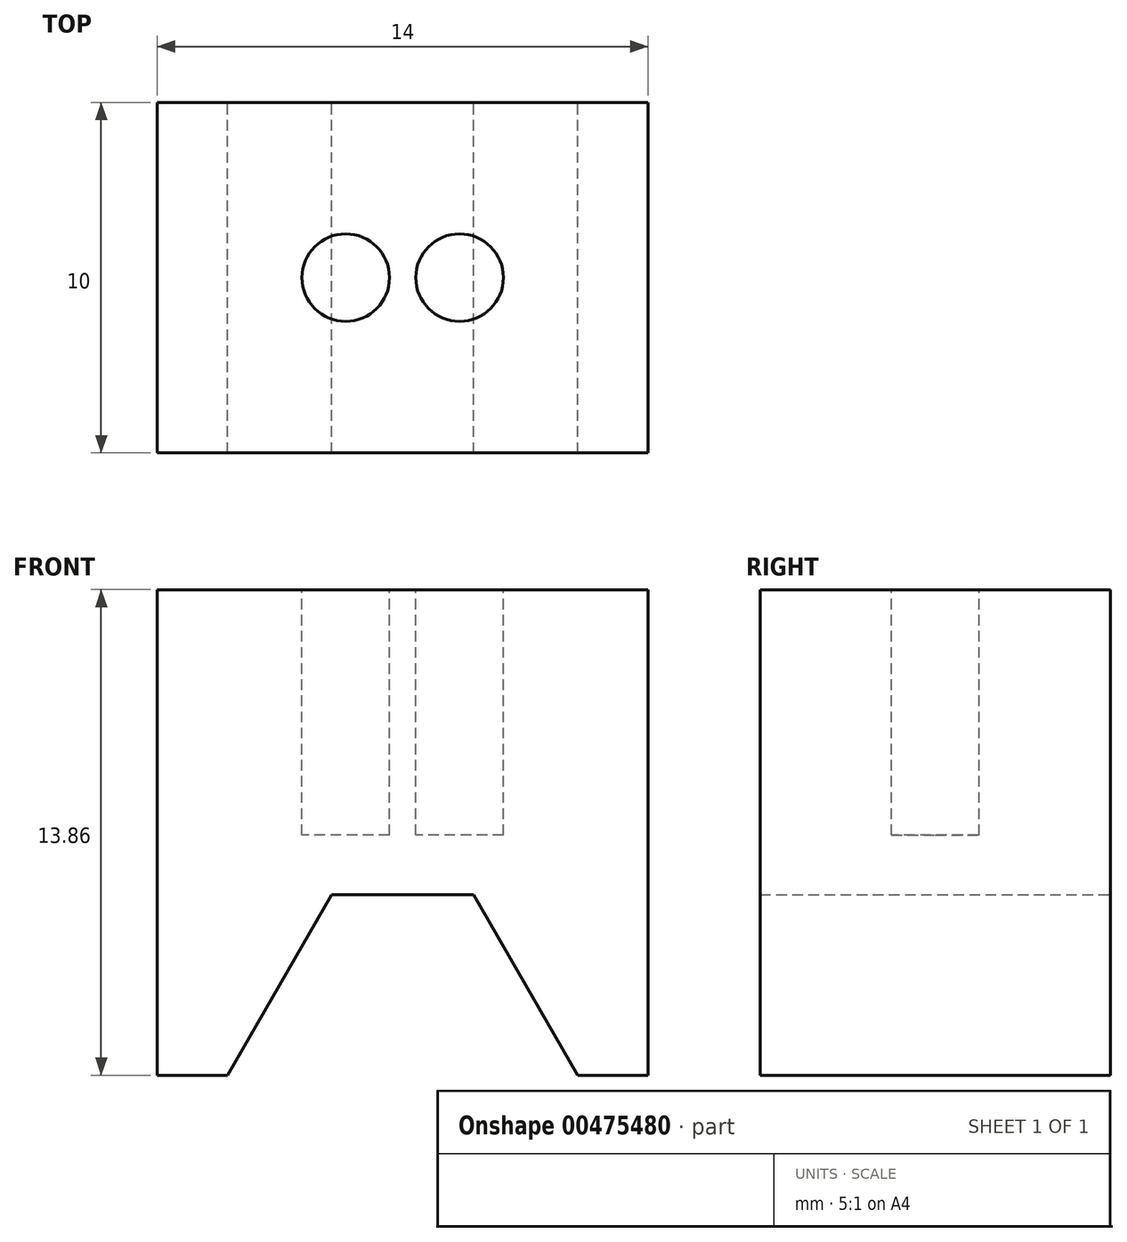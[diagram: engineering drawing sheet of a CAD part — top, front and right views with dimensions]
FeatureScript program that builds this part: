
annotation { "Feature Type Name" : "Feature", "Feature Type Description" : "" }
export const myFeature = defineFeature(function(context is Context, id is Id, definition is map)
    precondition{}
    {
        {
            var Q0;
            Q0=qCreatedBy(makeId("Front.planeOp"),FACE);
            var sketch = newSketch(context, id + "F0", { "sketchPlane" : qUnion([Q0])});
            skLineSegment(sketch, "E0", {"start": v(-5, 0) * mm, "end": v(-2.03, 5.15) * mm});
            skLineSegment(sketch, "E1", {"start": v(2.03, 5.15) * mm, "end": v(5, 0) * mm});
            skLineSegment(sketch, "E2", {"start": v(-4, 13.86) * mm, "end": v(4, 13.86) * mm});
            skLineSegment(sketch, "E3.bottom", {"start": v(-7, 13.86) * mm, "end": v(7, 13.86) * mm});
            skLineSegment(sketch, "E3.top", {"start": v(-7, 0) * mm, "end": v(7, 0) * mm});
            skLineSegment(sketch, "E3.left", {"start": v(-7, 13.86) * mm, "end": v(-7, 0) * mm});
            skLineSegment(sketch, "E3.right", {"start": v(7, 13.86) * mm, "end": v(7, 0) * mm});
            skCircle(sketch, "E4", {"center": v(0, 0) * mm, "radius": 5 * mm, "construction": true});
            skLineSegment(sketch, "E5", {"start": v(-2.03, 5.15) * mm, "end": v(2.03, 5.15) * mm});
            skPoint(sketch, "E6.orphan", {"position": v(0, 8.66) * mm});
            skSolve(sketch);
        }
        {
            var Q0;
            {var subQ1=sQuery(id+"F0.wireOp",EDGE,"E0");Q0=makeQuery(id+"F0.imprint","IMPRINT",FACE,{"disambiguationData":[TD([[makeQuery(id+"F0.imprint","IMPRINT",EDGE,{"derivedFrom":subQ1}),1.0]])]});}
            extrude(context, id + "F1", {"entities" : qUnion([Q0]), "depth" : 10 * mm, "offsetDistance" : 25 * mm});
        }
        {
            var Q0;
            Q0=makeQuery(id+"F1.opExtrude","SWEPT_FACE",FACE,{"disambiguationData":[OSD([sQuery(id+"F0.wireOp",EDGE,"E3.bottom")])]});
            var sketch = newSketch(context, id + "F2", { "sketchPlane" : qUnion([Q0])});
            skLineSegment(sketch, "E7", {"start": v(0, 0) * mm, "end": v(0, -10) * mm, "construction": true});
            skPoint(sketch, "E7.endSnap0", {"position": v(0, -10) * mm});
            skLineSegment(sketch, "E8", {"start": v(-1.62, -5) * mm, "end": v(1.63, -5) * mm, "construction": true});
            skPoint(sketch, "E8.startSnap0", {"position": v(0, -5) * mm});
            skCircle(sketch, "E9", {"center": v(1.63, -5) * mm, "radius": 1.25 * mm});
            skCircle(sketch, "E10", {"center": v(-1.62, -5) * mm, "radius": 1.25 * mm});
            skSolve(sketch);
        }
        {
            var Q0;
            Q0=makeQuery(id+"F2.imprint","IMPRINT",FACE,{"disambiguationData":[TD([[makeQuery(id+"F2.imprint","IMPRINT",EDGE,{"derivedFrom":sQuery(id+"F2.wireOp",EDGE,"E9")}),1.0]])]});
            var Q1;
            Q1=makeQuery(id+"F2.imprint","IMPRINT",FACE,{"disambiguationData":[TD([[makeQuery(id+"F2.imprint","IMPRINT",EDGE,{"derivedFrom":sQuery(id+"F2.wireOp",EDGE,"E10")}),1.0]])]});
            extrude(context, id + "F3", {"entities" : qUnion([Q0, Q1]), "operationType" : NewBodyOperationType.REMOVE, "oppositeDirection" : true, "depth" : 7 * mm, "offsetDistance" : 25 * mm});
        }
    });
